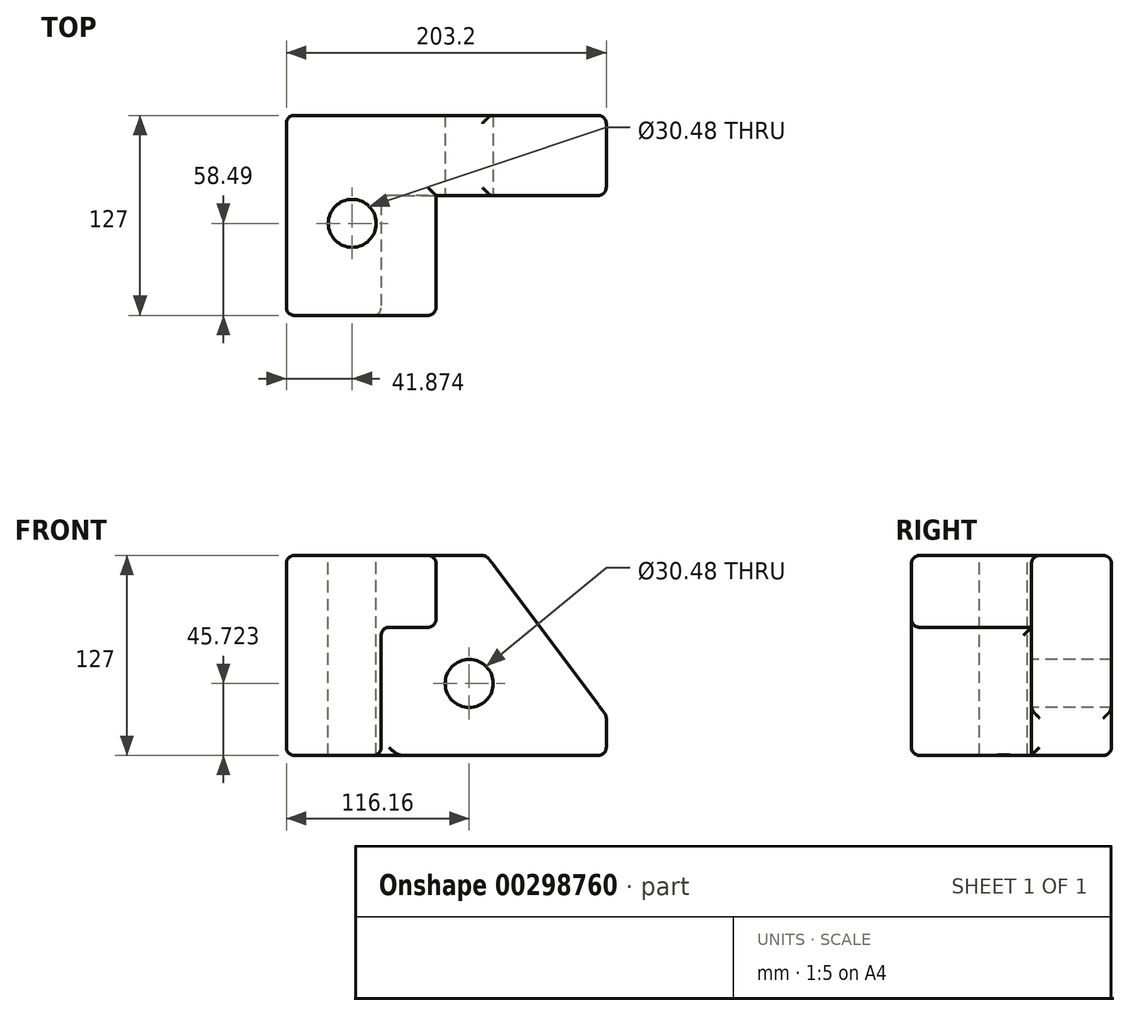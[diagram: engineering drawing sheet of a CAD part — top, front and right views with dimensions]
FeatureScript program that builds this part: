
annotation { "Feature Type Name" : "Feature", "Feature Type Description" : "" }
export const myFeature = defineFeature(function(context is Context, id is Id, definition is map)
    precondition{}
    {
        {
            var Q0;
            Q0=qCreatedBy(makeId("Front.planeOp"),FACE);
            var sketch = newSketch(context, id + "F0", { "sketchPlane" : qUnion([Q0])});
            skLineSegment(sketch, "E0.bottom", {"start": v(-60.28, 84.05) * mm, "end": v(142.92, 84.05) * mm});
            skLineSegment(sketch, "E0.top", {"start": v(-60.28, -42.95) * mm, "end": v(142.92, -42.95) * mm});
            skLineSegment(sketch, "E0.left", {"start": v(-60.28, 84.05) * mm, "end": v(-60.28, -42.95) * mm});
            skLineSegment(sketch, "E0.right", {"start": v(142.92, 84.05) * mm, "end": v(142.92, -42.95) * mm});
            skSolve(sketch);
        }
        {
            var Q0;
            Q0 = qSketchRegion(id + "F0", true);
            extrude(context, id + "F1", {"entities" : qUnion([Q0]), "depth" : 127 * mm});
        }
        {
            var Q0;
            Q0=makeQuery(id+"F1.opExtrude","CAP_FACE",FACE,{"disambiguationData":[OSD([sQuery(id+"F0.wireOp",EDGE,"E0.bottom"),sQuery(id+"F0.wireOp",EDGE,"E0.top"),sQuery(id+"F0.wireOp",EDGE,"E0.left"),sQuery(id+"F0.wireOp",EDGE,"E0.right")])],"isStart":false});
            var sketch = newSketch(context, id + "F2", { "sketchPlane" : qUnion([Q0])});
            skLineSegment(sketch, "E1", {"start": v(-60.28, -30.91) * mm, "end": v(-60.28, 84.05) * mm});
            skLineSegment(sketch, "E2", {"start": v(-60.28, 84.05) * mm, "end": v(-60.28, -42.95) * mm});
            skLineSegment(sketch, "E3", {"start": v(-60.28, 84.05) * mm, "end": v(34.82, 84.05) * mm});
            skLineSegment(sketch, "E4", {"start": v(34.82, 38.43) * mm, "end": v(34.82, 84.05) * mm});
            skLineSegment(sketch, "E5", {"start": v(34.82, 38.43) * mm, "end": v(0, 38.43) * mm});
            skLineSegment(sketch, "E6", {"start": v(0, 38.43) * mm, "end": v(0, -42.95) * mm});
            skLineSegment(sketch, "E7", {"start": v(34.82, 84.05) * mm, "end": v(34.82, 38.43) * mm});
            skLineSegment(sketch, "E8", {"start": v(-60.28, -42.95) * mm, "end": v(0, -42.95) * mm});
            skSolve(sketch);
        }
        {
            var Q0;
            Q0=makeQuery(id+"F2.imprint","IMPRINT",FACE,{"disambiguationData":[TD([[makeQuery(id+"F2.imprint","IMPRINT",EDGE,{"derivedFrom":sQuery(id+"F2.wireOp",EDGE,"E5")}),1.0]])]});
            extrude(context, id + "F3", {"entities" : qUnion([Q0]), "operationType" : NewBodyOperationType.REMOVE, "oppositeDirection" : true, "depth" : 76.2 * mm});
        }
        {
            var Q0;
            Q0=makeQuery(id+"F1.opExtrude","SWEPT_EDGE",EDGE,{"disambiguationData":[OSD([sQuery(id+"F0.wireOp",EDGE,"E0.bottom"),sQuery(id+"F0.wireOp",EDGE,"E0.right")])]});
            chamfer(context, id + "F4", {"entities" : qUnion([Q0]), "chamferType" : ChamferType.TWO_OFFSETS, "width1" : 76.2 * mm, "oppositeDirection" : false, "width2" : 101.6 * mm, "tangentPropagation" : true});
        }
        {
            var Q0;
            Q0=makeQuery(id+"F3.boolean.opBoolean","COPY",EDGE,{"derivedFrom":makeQuery(id+"F3.opExtrude","SWEPT_EDGE",EDGE,{"disambiguationData":[OSD([sQuery(id+"F0.wireOp",EDGE,"E0.bottom"),sQuery(id+"F2.wireOp",EDGE,"E3"),sQuery(id+"F2.wireOp",EDGE,"E7")])]})});
            var Q1;
            Q1=makeQuery(id+"F3.boolean.opBoolean","COPY",EDGE,{"derivedFrom":makeQuery(id+"F3.opExtrude","CAP_EDGE",EDGE,{"disambiguationData":[OSD([sQuery(id+"F2.wireOp",EDGE,"E6")])],"isStart":true})});
            var Q2;
            Q2=makeQuery(id+"F3.boolean.opBoolean","COPY",EDGE,{"derivedFrom":makeQuery(id+"F3.opExtrude","CAP_EDGE",EDGE,{"disambiguationData":[OSD([sQuery(id+"F0.wireOp",EDGE,"E0.bottom")])],"isStart":false})});
            var Q3;
            Q3=makeQuery(id+"F3.boolean.opBoolean","COPY",EDGE,{"derivedFrom":makeQuery(id+"F3.opExtrude","CAP_EDGE",EDGE,{"disambiguationData":[OSD([sQuery(id+"F2.wireOp",EDGE,"E7")])],"isStart":false})});
            var Q4;
            Q4=makeQuery(id+"F1.opExtrude","CAP_FACE",FACE,{"disambiguationData":[OSD([sQuery(id+"F0.wireOp",EDGE,"E0.bottom"),sQuery(id+"F0.wireOp",EDGE,"E0.top"),sQuery(id+"F0.wireOp",EDGE,"E0.left"),sQuery(id+"F0.wireOp",EDGE,"E0.right")])],"isStart":false});
            var Q5;
            Q5=makeQuery(id+"F1.opExtrude","SWEPT_FACE",FACE,{"disambiguationData":[OSD([sQuery(id+"F0.wireOp",EDGE,"E0.bottom")])]});
            var Q6;
            Q6=makeQuery(id+"F3.boolean.opBoolean","COPY",EDGE,{"derivedFrom":makeQuery(id+"F3.opExtrude","CAP_EDGE",EDGE,{"disambiguationData":[OSD([sQuery(id+"F2.wireOp",EDGE,"E6")])],"isStart":false})});
            var Q7;
            Q7=makeQuery(id+"F3.boolean.opBoolean","COPY",FACE,{"derivedFrom":makeQuery(id+"F3.opExtrude","SWEPT_FACE",FACE,{"disambiguationData":[OSD([sQuery(id+"F2.wireOp",EDGE,"E6")])]})});
            var Q8;
            Q8=makeQuery(id+"F1.opExtrude","SWEPT_FACE",FACE,{"disambiguationData":[OSD([sQuery(id+"F0.wireOp",EDGE,"E0.right")])]});
            var Q9;
            Q9=makeQuery(id+"F1.opExtrude","CAP_EDGE",EDGE,{"disambiguationData":[OSD([sQuery(id+"F0.wireOp",EDGE,"E0.top")])],"isStart":true});
            var Q10;
            Q10=makeQuery(id+"F1.opExtrude","CAP_EDGE",EDGE,{"disambiguationData":[OSD([sQuery(id+"F0.wireOp",EDGE,"E0.left")])],"isStart":true});
            var Q11;
            Q11=makeQuery(id+"F1.opExtrude","SWEPT_EDGE",EDGE,{"disambiguationData":[OSD([sQuery(id+"F0.wireOp",EDGE,"E0.top"),sQuery(id+"F0.wireOp",EDGE,"E0.left")])]});
            var Q12;
            Q12=makeQuery(id+"F3.boolean.opBoolean","COPY",EDGE,{"derivedFrom":makeQuery(id+"F3.opExtrude","SWEPT_EDGE",EDGE,{"disambiguationData":[OSD([sQuery(id+"F2.wireOp",EDGE,"E5"),sQuery(id+"F2.wireOp",EDGE,"E7")])]})});
            fillet(context, id + "F5", {"entities" : qUnion([Q0, Q1, Q2, Q3, Q4, Q5, Q6, Q7, Q8, Q9, Q10, Q11, Q12]), "radius" : 5.08 * mm, "tangentPropagation" : true, "allowEdgeOverflow" : false});
        }
        {
            var Q0;
            Q0=makeQuery(id+"F3.boolean.opBoolean","COPY",FACE,{"derivedFrom":makeQuery(id+"F3.opExtrude","CAP_FACE",FACE,{"disambiguationData":[OSD([sQuery(id+"F0.wireOp",EDGE,"E0.bottom"),sQuery(id+"F0.wireOp",EDGE,"E0.top"),sQuery(id+"F0.wireOp",EDGE,"E0.right"),sQuery(id+"F2.wireOp",EDGE,"E5"),sQuery(id+"F2.wireOp",EDGE,"E6"),sQuery(id+"F2.wireOp",EDGE,"E7")])],"isStart":false})});
            var sketch = newSketch(context, id + "F6", { "sketchPlane" : qUnion([Q0])});
            skCircle(sketch, "E9", {"center": v(55.88, 2.77) * mm, "radius": 15.24 * mm});
            skSolve(sketch);
        }
        {
            var Q0;
            Q0=makeQuery(id+"F6.imprint","IMPRINT",FACE,{"disambiguationData":[TD([[makeQuery(id+"F6.imprint","IMPRINT",EDGE,{"derivedFrom":sQuery(id+"F6.wireOp",EDGE,"E9")}),1.0]])]});
            var Q1;
            Q1=sQuery(id+"F6.wireOp",EDGE,"E9");
            var Q2;
            Q2=makeQuery(id+"F1.opExtrude","CAP_FACE",FACE,{"disambiguationData":[OSD([sQuery(id+"F0.wireOp",EDGE,"E0.bottom"),sQuery(id+"F0.wireOp",EDGE,"E0.top"),sQuery(id+"F0.wireOp",EDGE,"E0.left"),sQuery(id+"F0.wireOp",EDGE,"E0.right")])],"isStart":true});
            extrude(context, id + "F7", {"entities" : qUnion([Q0]), "operationType" : NewBodyOperationType.REMOVE, "surfaceEntities" : qUnion([Q1]), "endBound" : BoundingType.UP_TO_SURFACE, "oppositeDirection" : true, "endBoundEntityFace" : qUnion([Q2]), "depth" : 25.4 * mm});
        }
        {
            var Q0;
            Q0=makeQuery(id+"F1.opExtrude","SWEPT_FACE",FACE,{"disambiguationData":[OSD([sQuery(id+"F0.wireOp",EDGE,"E0.bottom")])]});
            var sketch = newSketch(context, id + "F8", { "sketchPlane" : qUnion([Q0])});
            skCircle(sketch, "E10", {"center": v(-18.4, -68.5) * mm, "radius": 15.24 * mm});
            skSolve(sketch);
        }
        {
            var Q0;
            Q0=makeQuery(id+"F8.imprint","IMPRINT",FACE,{"disambiguationData":[TD([[makeQuery(id+"F8.imprint","IMPRINT",EDGE,{"derivedFrom":sQuery(id+"F8.wireOp",EDGE,"E10")}),1.0]])]});
            var Q1;
            Q1=makeQuery(id+"F1.opExtrude","SWEPT_FACE",FACE,{"disambiguationData":[OSD([sQuery(id+"F0.wireOp",EDGE,"E0.top")])]});
            extrude(context, id + "F9", {"entities" : qUnion([Q0]), "operationType" : NewBodyOperationType.REMOVE, "endBound" : BoundingType.UP_TO_SURFACE, "oppositeDirection" : true, "endBoundEntityFace" : qUnion([Q1]), "depth" : 25.4 * mm});
        }
    });
